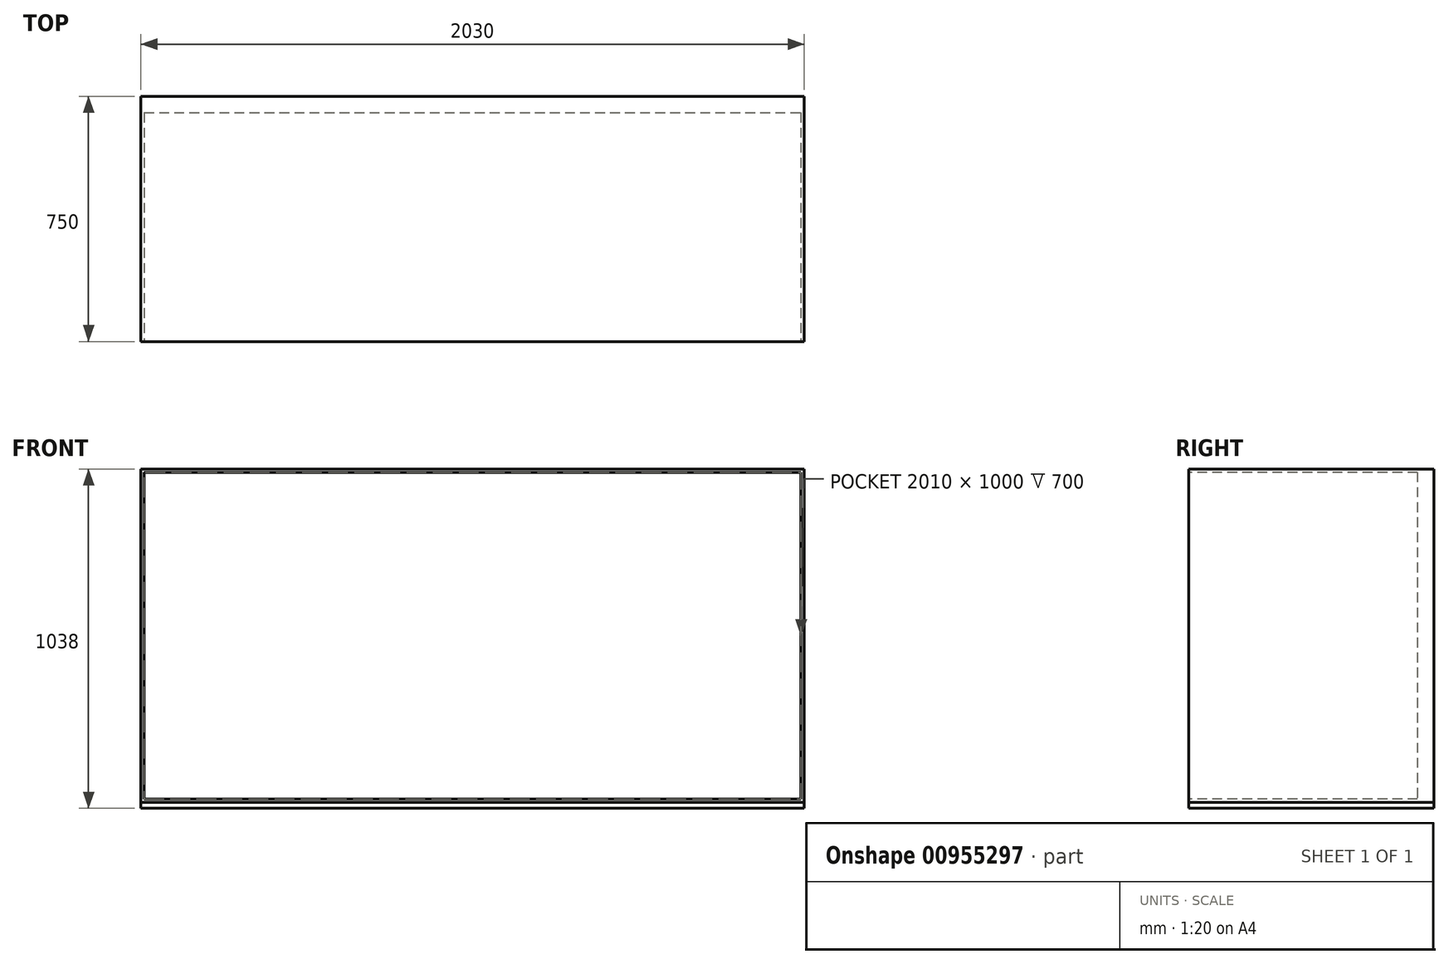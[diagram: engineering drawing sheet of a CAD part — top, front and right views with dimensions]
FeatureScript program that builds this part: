
annotation { "Feature Type Name" : "Feature", "Feature Type Description" : "" }
export const myFeature = defineFeature(function(context is Context, id is Id, definition is map)
    precondition{}
    {
        {
            var Q0;
            Q0=qCreatedBy(makeId("Front.planeOp"),FACE);
            var sketch = newSketch(context, id + "F0", { "sketchPlane" : qUnion([Q0])});
            skLineSegment(sketch, "E0.bottom", {"start": v(-1015, 510) * mm, "end": v(1015, 510) * mm});
            skLineSegment(sketch, "E0.top", {"start": v(-1015, -510) * mm, "end": v(1015, -510) * mm});
            skLineSegment(sketch, "E0.left", {"start": v(-1015, 510) * mm, "end": v(-1015, -510) * mm});
            skLineSegment(sketch, "E0.right", {"start": v(1015, 510) * mm, "end": v(1015, -510) * mm});
            skPoint(sketch, "E0.middle", {"position": v(0, 0) * mm});
            skSolve(sketch);
        }
        {
            var Q0;
            Q0 = qSketchRegion(id + "F0", true);
            extrude(context, id + "F1", {"entities" : qUnion([Q0]), "depth" : 750 * mm, "offsetDistance" : 25 * mm});
        }
        {
            var Q0;
            Q0=makeQuery(id+"F1.opExtrude","CAP_FACE",FACE,{"disambiguationData":[OSD([sQuery(id+"F0.wireOp",EDGE,"E0.bottom"),sQuery(id+"F0.wireOp",EDGE,"E0.top"),sQuery(id+"F0.wireOp",EDGE,"E0.left"),sQuery(id+"F0.wireOp",EDGE,"E0.right")])],"isStart":false});
            var sketch = newSketch(context, id + "F2", { "sketchPlane" : qUnion([Q0])});
            skLineSegment(sketch, "E1.bottom", {"start": v(-1005, 500) * mm, "end": v(1005, 500) * mm});
            skLineSegment(sketch, "E1.top", {"start": v(-1005, -500) * mm, "end": v(1005, -500) * mm});
            skLineSegment(sketch, "E1.left", {"start": v(-1005, 500) * mm, "end": v(-1005, -500) * mm});
            skLineSegment(sketch, "E1.right", {"start": v(1005, 500) * mm, "end": v(1005, -500) * mm});
            skPoint(sketch, "E1.middle", {"position": v(0, 0) * mm});
            skSolve(sketch);
        }
        {
            var Q0;
            Q0 = qSketchRegion(id + "F2", true);
            extrude(context, id + "F3", {"entities" : qUnion([Q0]), "operationType" : NewBodyOperationType.REMOVE, "oppositeDirection" : true, "depth" : 700 * mm, "offsetDistance" : 25 * mm});
        }
        {
            var Q0;
            Q0=makeQuery(id+"F1.opExtrude","SWEPT_FACE",FACE,{"disambiguationData":[OSD([sQuery(id+"F0.wireOp",EDGE,"E0.top")])]});
            var sketch = newSketch(context, id + "F4", { "sketchPlane" : qUnion([Q0])});
            skLineSegment(sketch, "E2.bottom", {"start": v(-1015, 750) * mm, "end": v(1015, 750) * mm});
            skLineSegment(sketch, "E2.top", {"start": v(-1015, 0) * mm, "end": v(1015, 0) * mm});
            skLineSegment(sketch, "E2.left", {"start": v(-1015, 750) * mm, "end": v(-1015, 0) * mm});
            skLineSegment(sketch, "E2.right", {"start": v(1015, 750) * mm, "end": v(1015, 0) * mm});
            skPoint(sketch, "E2.middle", {"position": v(0, 375) * mm});
            skPoint(sketch, "E2.middle.positionSnap0", {"position": v(-1015, 375) * mm});
            skPoint(sketch, "E2.centerSnap0", {"position": v(-1015, 375) * mm});
            skSolve(sketch);
        }
        {
            var Q0;
            Q0 = qSketchRegion(id + "F4", true);
            extrude(context, id + "F5", {"entities" : qUnion([Q0]), "depth" : 18 * mm, "offsetDistance" : 25 * mm});
        }
    });
